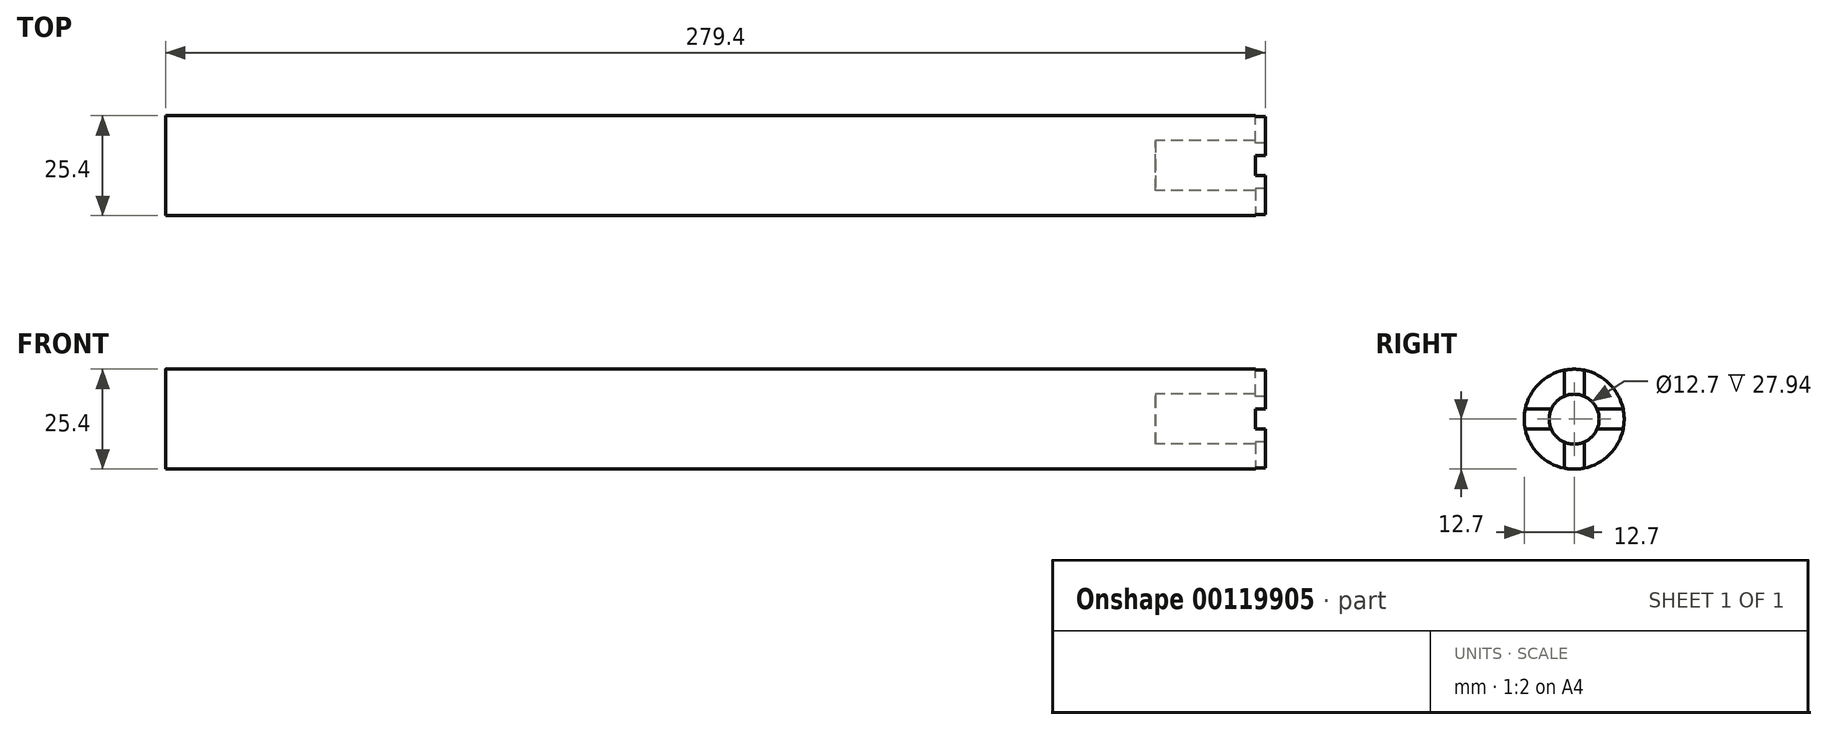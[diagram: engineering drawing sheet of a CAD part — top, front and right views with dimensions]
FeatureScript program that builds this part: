
annotation { "Feature Type Name" : "Feature", "Feature Type Description" : "" }
export const myFeature = defineFeature(function(context is Context, id is Id, definition is map)
    precondition{}
    {
        {
            var Q0;
            Q0=qCreatedBy(makeId("Right.planeOp"),FACE);
            var sketch = newSketch(context, id + "F0", { "sketchPlane" : qUnion([Q0])});
            skCircle(sketch, "E0", {"center": v(0, 0) * mm, "radius": 12.7 * mm});
            skSolve(sketch);
        }
        {
            var Q0;
            Q0=qSketchRegion(id+"F0",true);
            var Q1;
            Q1=makeQuery(id+"F0.imprint","IMPRINT",FACE,{"disambiguationData":[TD([[makeQuery(id+"F0.imprint","IMPRINT",EDGE,{"derivedFrom":sQuery(id+"F0.wireOp",EDGE,"E0")}),1.0]])]});
            extrude(context, id + "F1", {"entities" : qUnion([Q0, Q1]), "depth" : 276.86 * mm});
        }
        {
            var Q0;
            Q0=makeQuery(id+"F1.opExtrude","CAP_FACE",FACE,{"disambiguationData":[OSD([sQuery(id+"F0.wireOp",EDGE,"E0")])],"isStart":false});
            var sketch = newSketch(context, id + "F2", { "sketchPlane" : qUnion([Q0])});
            skCircle(sketch, "E1", {"center": v(0, 0) * mm, "radius": 6.35 * mm});
            skLineSegment(sketch, "E2", {"start": v(0, 12.7) * mm, "end": v(0, 6.35) * mm, "construction": true});
            skLineSegment(sketch, "E3", {"start": v(-12.7, 0) * mm, "end": v(-6.35, 0) * mm, "construction": true});
            skLineSegment(sketch, "E4", {"start": v(-2.54, -5.82) * mm, "end": v(-2.54, -12.44) * mm});
            skLineSegment(sketch, "E5", {"start": v(2.54, -5.82) * mm, "end": v(2.54, -12.44) * mm});
            skLineSegment(sketch, "E6", {"start": v(-2.54, 5.82) * mm, "end": v(-2.54, 12.44) * mm});
            skLineSegment(sketch, "E7", {"start": v(2.54, 5.82) * mm, "end": v(2.54, 12.44) * mm});
            skLineSegment(sketch, "E8", {"start": v(5.82, 2.54) * mm, "end": v(12.44, 2.54) * mm});
            skLineSegment(sketch, "E9", {"start": v(5.82, -2.54) * mm, "end": v(12.44, -2.54) * mm});
            skLineSegment(sketch, "E10", {"start": v(-5.82, 2.54) * mm, "end": v(-12.44, 2.54) * mm});
            skLineSegment(sketch, "E11", {"start": v(-5.82, -2.54) * mm, "end": v(-12.44, -2.54) * mm});
            skLineSegment(sketch, "E12.trimOffspring", {"start": v(0, -6.35) * mm, "end": v(0, -12.7) * mm, "construction": true});
            skLineSegment(sketch, "E13.trimOffspring", {"start": v(6.35, 0) * mm, "end": v(12.7, 0) * mm, "construction": true});
            skSolve(sketch);
        }
        {
            var Q0;
            {var subQ0=sQuery(id+"F2.wireOp",EDGE,"E7");Q0=makeQuery(id+"F2.imprint","IMPRINT",FACE,{"disambiguationData":[TD([[makeQuery(id+"F2.imprint","IMPRINT",EDGE,{"derivedFrom":subQ0}),-1.0]])]});}
            var Q1;
            {var subQ0=sQuery(id+"F2.wireOp",EDGE,"E6");Q1=makeQuery(id+"F2.imprint","IMPRINT",FACE,{"disambiguationData":[TD([[makeQuery(id+"F2.imprint","IMPRINT",EDGE,{"derivedFrom":subQ0}),1.0]])]});}
            var Q2;
            {var subQ0=sQuery(id+"F2.wireOp",EDGE,"E4");Q2=makeQuery(id+"F2.imprint","IMPRINT",FACE,{"disambiguationData":[TD([[makeQuery(id+"F2.imprint","IMPRINT",EDGE,{"derivedFrom":subQ0}),-1.0]])]});}
            var Q3;
            {var subQ0=sQuery(id+"F2.wireOp",EDGE,"E5");Q3=makeQuery(id+"F2.imprint","IMPRINT",FACE,{"disambiguationData":[TD([[makeQuery(id+"F2.imprint","IMPRINT",EDGE,{"derivedFrom":subQ0}),1.0]])]});}
            extrude(context, id + "F3", {"entities" : qUnion([Q0, Q1, Q2, Q3]), "operationType" : NewBodyOperationType.ADD, "depth" : 2.54 * mm});
        }
        {
            var Q0;
            {var subQ0=sQuery(id+"F2.wireOp",EDGE,"E1");var subQ4=makeQuery(id+"F2.imprint","INTERSECT",VERTEX,{"derivedFrom":[subQ0,sQuery(id+"F2.wireOp",EDGE,"E7")]});Q0=makeQuery(id+"F2.imprint","IMPRINT",FACE,{"disambiguationData":[TD([[makeQuery(id+"F2.imprint","IMPRINT",EDGE,{"disambiguationData":[TD([[subQ4,1.0]])],"derivedFrom":subQ0}),1.0]])]});}
            extrude(context, id + "F4", {"entities" : qUnion([Q0]), "operationType" : NewBodyOperationType.REMOVE, "oppositeDirection" : true, "depth" : 25.4 * mm});
        }
    });
